# Revit family: DC_Holyoake_OutsideLouver_OHCL-C-102_supply_12
name_source: partatom
category: Air Terminals
revit_build: Autodesk Revit 2013 (Build: 20120221_2030(x64)
units: mm (PartAtom-declared; Revit-internal decimal feet)

## types (2) — shared parameters
Accessories = Aluminium Bird mesh or insect mesh (fibreglass)
Blade Height = 134.9 mm  [stored 0.442585 ft]
Blade Offset = 0.9 mm
Blade Pitch = 102 mm
Blade Width = 101.4 mm  [stored 0.332677 ft]
Channel Thickness = 103.2 mm  [stored 0.338583 ft]
Channel Width = 25.4 mm  [stored 0.0833333 ft]
Clearance Min. = 300 mm  [stored 0.984252 ft]
Description = Holyoake Outside Horizontal Louvre
Gang Bar Width (plus min. 300mm clearance) = 50 mm  [stored 0.164042 ft]
Gang Bar With Actuator Width (plus min. 300mm clearance) = 150 mm  [stored 0.492126 ft]
Manufacturer = Holyoake Industries Limited
Material - Body = Holyoake Aluminium
Material - Face = Holyoake Aluminium
Max Flow = 5000.0 L/s
Min Flow = 100.0 L/s
Overall Depth = 38.3 mm  [stored 0.125656 ft]
Static Pressure Max = 60.0 Pa
Static Pressure Min = 10.0 Pa
Type Comments = 102mm Horizontal Curved Profile Louvers in Channel Surround

## per-type parameters (varying)
| type | Blade Array Count | Blade Control | Blade Count | Blade Cut Setout | Blade Length | Connector Height | Connector Width | Exact Neck Height | Exact Neck Width | Holyoake Product Range | Nominal Height | Nominal Width | Overall Opening | Top Blade Height | URL |
| OHL-C-102 | 6.952941 | No | 6 | 612 mm  [stored 2.00787 ft] | 684.2 mm  [stored 2.24475 ft] | 685.2 mm  [stored 2.24803 ft] | 660.2 mm  [stored 2.16601 ft] | 760 mm | 735 mm  [stored 2.41142 ft] |  | 766 mm  [stored 2.51312 ft] | 741 mm  [stored 2.4311 ft] | 709.2 mm | 97.2 mm | http://www.productspec.net |
| OHCL-C-102 | 7.541176 | Yes | 7 | 714 mm | 699.2 mm  [stored 2.29396 ft] | 745.2 mm | 675.2 mm  [stored 2.21522 ft] | 820 mm  [stored 2.69029 ft] | 750 mm  [stored 2.46063 ft] | Outside Louvres | 826 mm  [stored 2.70997 ft] | 756 mm  [stored 2.48031 ft] | 769.2 mm  [stored 2.52362 ft] | 55.2 mm | http://www.holyoake.com |

note: column(s) folded — value = type name in every type: Model

note: [stored X ft] marks values corroborated as IEEE doubles in the binary element streams (Revit-internal decimal feet)

## geometry (parser evidence)
native form markers: Blend x4, Sweep x11
no freeform markers — native parametric forms only
